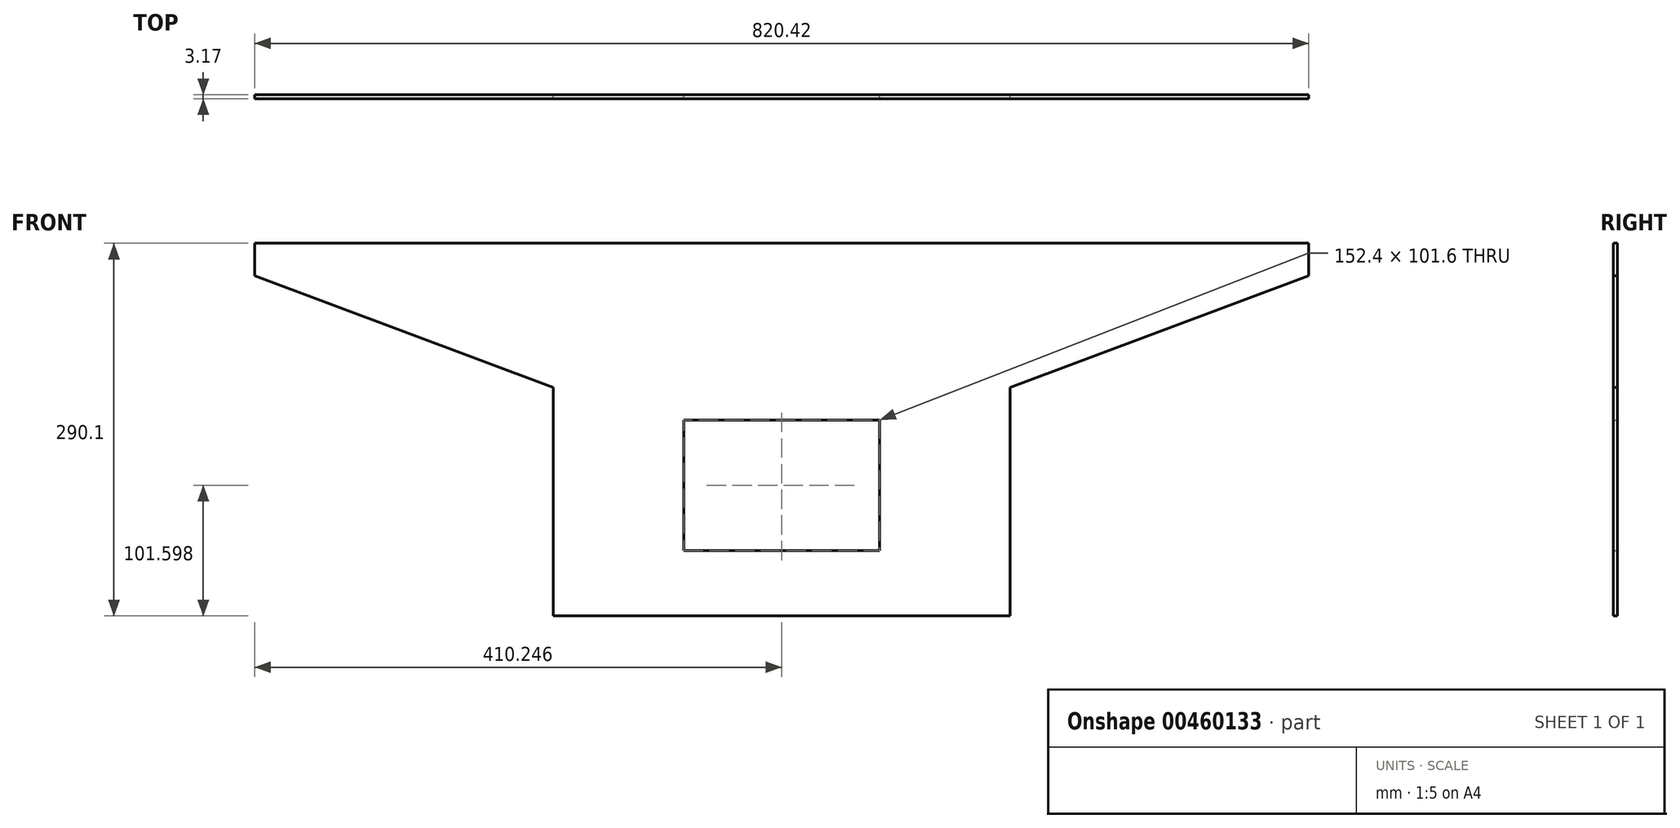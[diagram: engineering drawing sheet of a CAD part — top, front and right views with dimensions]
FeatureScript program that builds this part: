
annotation { "Feature Type Name" : "Feature", "Feature Type Description" : "" }
export const myFeature = defineFeature(function(context is Context, id is Id, definition is map)
    precondition{}
    {
        {
            var Q0;
            Q0=qCreatedBy(makeId("Front.planeOp"),FACE);
            var sketch = newSketch(context, id + "F0", { "sketchPlane" : qUnion([Q0])});
            skLineSegment(sketch, "E0", {"start": v(-403.59, 7.58) * mm, "end": v(416.83, 7.58) * mm});
            skLineSegment(sketch, "E1", {"start": v(-403.59, 7.58) * mm, "end": v(-403.59, -17.82) * mm});
            skLineSegment(sketch, "E2", {"start": v(-403.59, -17.82) * mm, "end": v(-171.14, -104.72) * mm});
            skLineSegment(sketch, "E3", {"start": v(-171.14, -104.72) * mm, "end": v(-171.14, 0) * mm, "construction": true});
            skLineSegment(sketch, "E4.top", {"start": v(-171.14, -282.52) * mm, "end": v(184.46, -282.52) * mm});
            skLineSegment(sketch, "E4.left", {"start": v(-171.14, -104.72) * mm, "end": v(-171.14, -282.52) * mm});
            skLineSegment(sketch, "E4.right", {"start": v(184.46, -104.72) * mm, "end": v(184.46, -282.52) * mm});
            skLineSegment(sketch, "E5", {"start": v(416.83, 7.58) * mm, "end": v(416.83, -17.82) * mm});
            skLineSegment(sketch, "E6", {"start": v(416.83, -17.82) * mm, "end": v(184.46, -104.72) * mm});
            skLineSegment(sketch, "E7.bottom", {"start": v(-69.54, -130.12) * mm, "end": v(82.86, -130.12) * mm});
            skLineSegment(sketch, "E7.top", {"start": v(-69.54, -231.72) * mm, "end": v(82.86, -231.72) * mm});
            skLineSegment(sketch, "E7.left", {"start": v(-69.54, -130.12) * mm, "end": v(-69.54, -231.72) * mm});
            skLineSegment(sketch, "E7.right", {"start": v(82.86, -130.12) * mm, "end": v(82.86, -231.72) * mm});
            skSolve(sketch);
        }
        {
            var Q0;
            Q0=makeQuery(id+"F0.imprint","IMPRINT",FACE,{"disambiguationData":[TD([[makeQuery(id+"F0.imprint","IMPRINT",EDGE,{"derivedFrom":sQuery(id+"F0.wireOp",EDGE,"E0")}),-1.0]])]});
            extrude(context, id + "F1", {"entities" : qUnion([Q0]), "depth" : 3.17 * mm});
        }
    });
